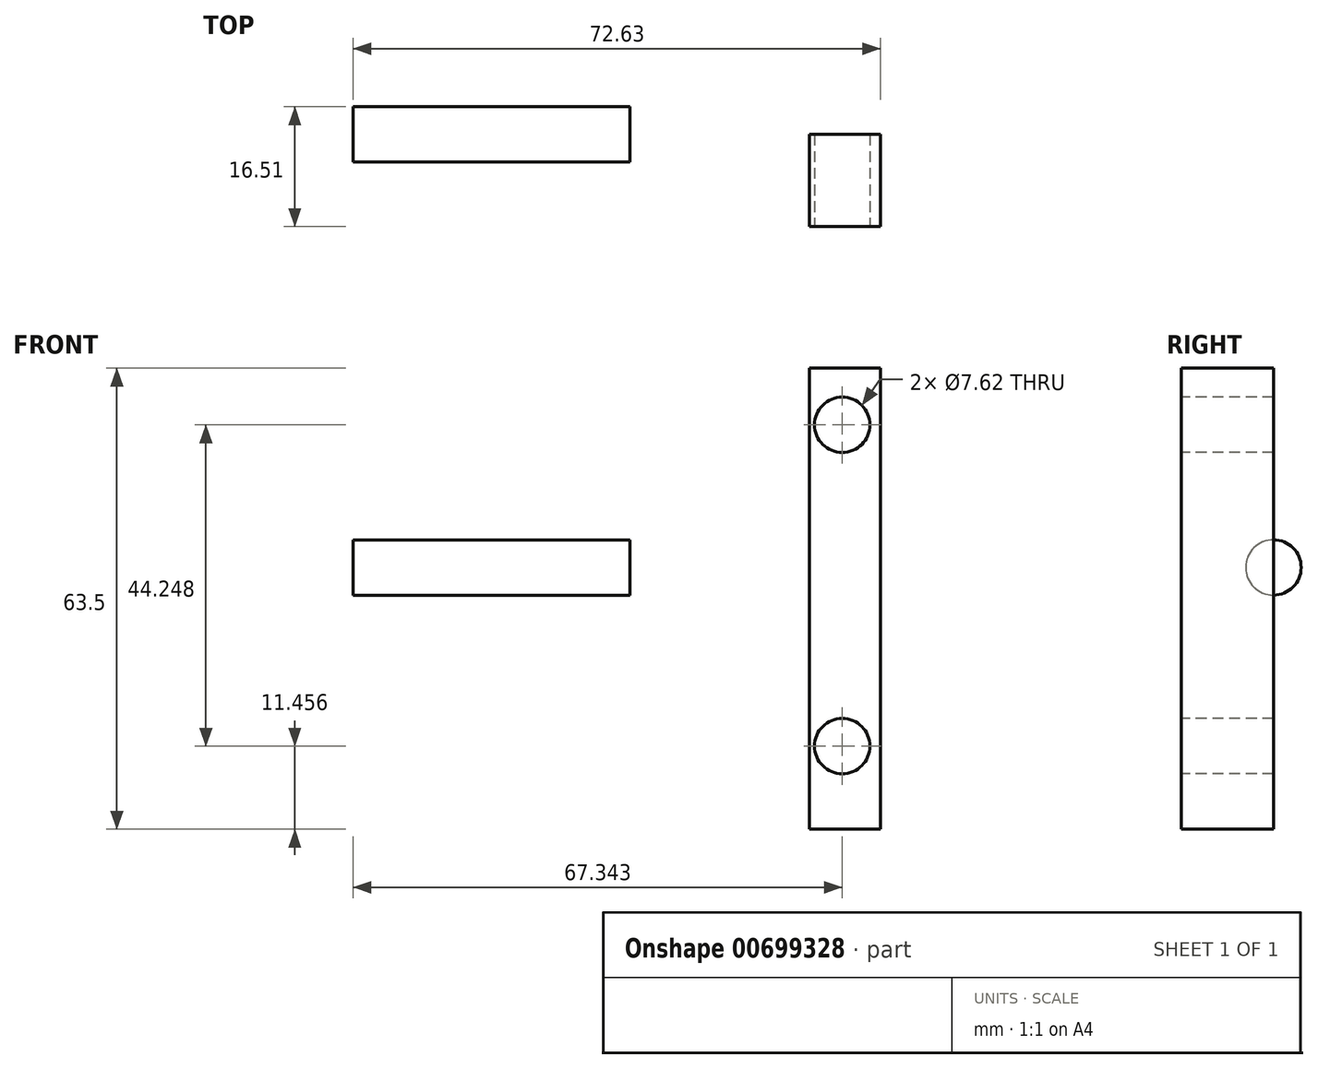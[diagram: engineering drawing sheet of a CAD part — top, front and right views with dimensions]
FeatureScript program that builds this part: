
annotation { "Feature Type Name" : "Feature", "Feature Type Description" : "" }
export const myFeature = defineFeature(function(context is Context, id is Id, definition is map)
    precondition{}
    {
        {
            var Q0;
            Q0=qCreatedBy(makeId("Right.planeOp"),FACE);
            var sketch = newSketch(context, id + "F0", { "sketchPlane" : qUnion([Q0])});
            skCircle(sketch, "E0", {"center": v(0, 0) * mm, "radius": 3.81 * mm});
            skSolve(sketch);
        }
        {
            var Q0;
            Q0 = qSketchRegion(id + "F0", true);
            extrude(context, id + "F1", {"entities" : qUnion([Q0]), "oppositeDirection" : true, "depth" : 38.1 * mm, "offsetDistance" : 25.4 * mm});
        }
        {
            var Q0;
            Q0=qCreatedBy(makeId("Front.planeOp"),FACE);
            var sketch = newSketch(context, id + "F2", { "sketchPlane" : qUnion([Q0])});
            skLineSegment(sketch, "E1.bottom", {"start": v(34.53, 27.44) * mm, "end": v(24.75, 27.44) * mm});
            skLineSegment(sketch, "E1.top", {"start": v(34.53, -36.06) * mm, "end": v(24.75, -36.06) * mm});
            skLineSegment(sketch, "E1.left", {"start": v(34.53, 27.44) * mm, "end": v(34.53, -36.06) * mm});
            skLineSegment(sketch, "E1.right", {"start": v(24.75, 27.44) * mm, "end": v(24.75, -36.06) * mm});
            skSolve(sketch);
        }
        {
            var Q0;
            Q0 = qSketchRegion(id + "F2", true);
            extrude(context, id + "F3", {"entities" : qUnion([Q0]), "depth" : 12.7 * mm, "offsetDistance" : 25.4 * mm});
        }
        {
            var Q0;
            Q0=makeQuery(id+"F3.opExtrude","CAP_FACE",FACE,{"disambiguationData":[OSD([sQuery(id+"F2.wireOp",EDGE,"E1.bottom"),sQuery(id+"F2.wireOp",EDGE,"E1.top"),sQuery(id+"F2.wireOp",EDGE,"E1.left"),sQuery(id+"F2.wireOp",EDGE,"E1.right")])],"isStart":false});
            var sketch = newSketch(context, id + "F4", { "sketchPlane" : qUnion([Q0])});
            skCircle(sketch, "E2", {"center": v(29.24, 19.64) * mm, "radius": 3.81 * mm});
            skCircle(sketch, "E3", {"center": v(29.24, -24.6) * mm, "radius": 3.81 * mm});
            skSolve(sketch);
        }
        {
            var Q0;
            Q0 = qSketchRegion(id + "F4", true);
            extrude(context, id + "F5", {"entities" : qUnion([Q0]), "operationType" : NewBodyOperationType.REMOVE, "oppositeDirection" : true, "depth" : 25.4 * mm, "offsetDistance" : 25.4 * mm});
        }
    });
